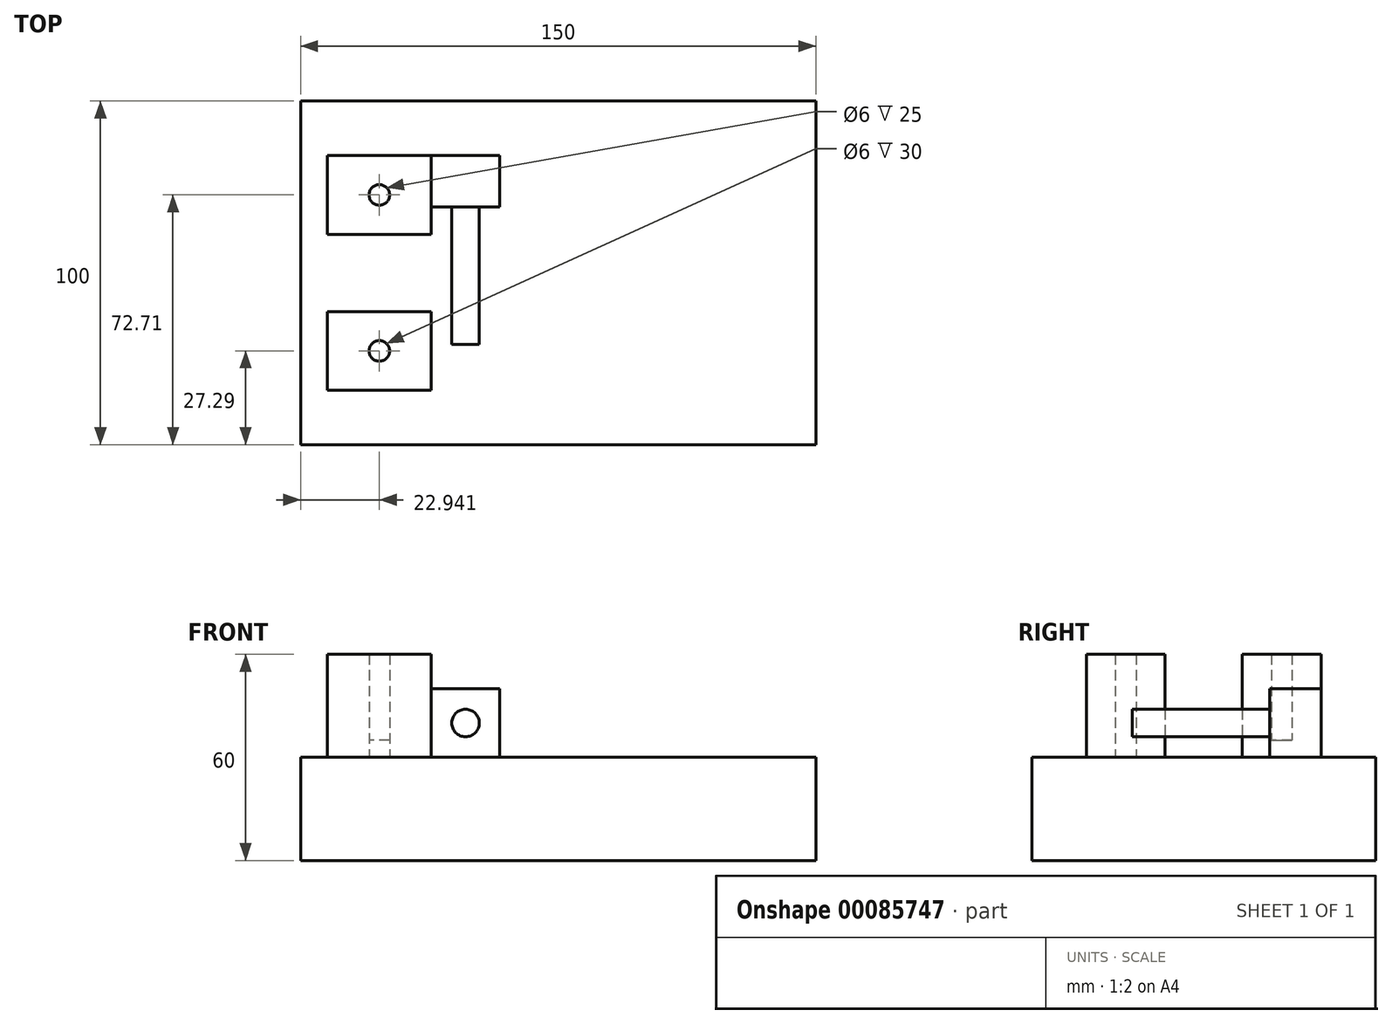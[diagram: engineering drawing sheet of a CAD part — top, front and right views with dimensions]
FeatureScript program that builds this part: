
annotation { "Feature Type Name" : "Feature", "Feature Type Description" : "" }
export const myFeature = defineFeature(function(context is Context, id is Id, definition is map)
    precondition{}
    {
        {
            var Q0;
            Q0=qCreatedBy(makeId("Top.planeOp"),FACE);
            var sketch = newSketch(context, id + "F0", { "sketchPlane" : qUnion([Q0])});
            skLineSegment(sketch, "E0.bottom", {"start": v(75, 50) * mm, "end": v(-75, 50) * mm});
            skLineSegment(sketch, "E0.top", {"start": v(75, -50) * mm, "end": v(-75, -50) * mm});
            skLineSegment(sketch, "E0.left", {"start": v(75, 50) * mm, "end": v(75, -50) * mm});
            skLineSegment(sketch, "E0.right", {"start": v(-75, 50) * mm, "end": v(-75, -50) * mm});
            skPoint(sketch, "E0.middle", {"position": v(0, 0) * mm});
            skSolve(sketch);
        }
        {
            var Q0;
            Q0=makeQuery(id+"F0.imprint","IMPRINT",FACE,{"disambiguationData":[TD([[makeQuery(id+"F0.imprint","IMPRINT",EDGE,{"derivedFrom":sQuery(id+"F0.wireOp",EDGE,"E0.bottom")}),1.0]])]});
            extrude(context, id + "F1", {"entities" : qUnion([Q0]), "depth" : 30 * mm});
        }
        {
            var Q0;
            Q0=makeQuery(id+"F1.opExtrude","CAP_FACE",FACE,{"disambiguationData":[OSD([sQuery(id+"F0.wireOp",EDGE,"E0.bottom"),sQuery(id+"F0.wireOp",EDGE,"E0.top"),sQuery(id+"F0.wireOp",EDGE,"E0.left"),sQuery(id+"F0.wireOp",EDGE,"E0.right")])],"isStart":false});
            var sketch = newSketch(context, id + "F2", { "sketchPlane" : qUnion([Q0])});
            skCircle(sketch, "E1", {"center": v(-52.06, 22.71) * mm, "radius": 3 * mm});
            skLineSegment(sketch, "E2", {"start": v(0, 0) * mm, "end": v(-75, 0) * mm});
            skCircle(sketch, "E3.MirrorC", {"center": v(-52.06, -22.71) * mm, "radius": 3 * mm});
            skLineSegment(sketch, "E4.bottom", {"start": v(-36.98, 34.17) * mm, "end": v(-67.14, 34.17) * mm});
            skLineSegment(sketch, "E4.top", {"start": v(-36.98, 11.25) * mm, "end": v(-67.14, 11.25) * mm});
            skLineSegment(sketch, "E4.left", {"start": v(-36.98, 34.17) * mm, "end": v(-36.98, 11.25) * mm});
            skLineSegment(sketch, "E4.right", {"start": v(-67.14, 34.17) * mm, "end": v(-67.14, 11.25) * mm});
            skLineSegment(sketch, "E5.MirrorCS", {"start": v(-36.98, -11.25) * mm, "end": v(-67.14, -11.25) * mm});
            skLineSegment(sketch, "E6.MirrorCS", {"start": v(-67.14, -34.17) * mm, "end": v(-67.14, -11.25) * mm});
            skLineSegment(sketch, "E7.MirrorCS", {"start": v(-36.98, -34.17) * mm, "end": v(-67.14, -34.17) * mm});
            skLineSegment(sketch, "E8.MirrorCS", {"start": v(-36.98, -34.17) * mm, "end": v(-36.98, -11.25) * mm});
            skSolve(sketch);
        }
        {
            var Q0;
            Q0=makeQuery(id+"F2.imprint","IMPRINT",FACE,{"disambiguationData":[TD([[makeQuery(id+"F2.imprint","IMPRINT",EDGE,{"derivedFrom":sQuery(id+"F2.wireOp",EDGE,"E3.MirrorC")}),-1.0]])]});
            var Q1;
            Q1=makeQuery(id+"F2.imprint","IMPRINT",FACE,{"disambiguationData":[TD([[makeQuery(id+"F2.imprint","IMPRINT",EDGE,{"derivedFrom":sQuery(id+"F2.wireOp",EDGE,"E1")}),1.0]])]});
            extrude(context, id + "F3", {"entities" : qUnion([Q0, Q1]), "operationType" : NewBodyOperationType.ADD, "depth" : 5 * mm});
        }
        {
            var Q0;
            Q0 = qSketchRegion(id + "F2", true);
            extrude(context, id + "F4", {"entities" : qUnion([Q0]), "operationType" : NewBodyOperationType.ADD, "depth" : 30 * mm});
        }
        {
            var Q0;
            Q0=makeQuery(id+"F4.opExtrude","SWEPT_FACE",FACE,{"disambiguationData":[OSD([sQuery(id+"F2.wireOp",EDGE,"E4.bottom")])]});
            var sketch = newSketch(context, id + "F5", { "sketchPlane" : qUnion([Q0])});
            skLineSegment(sketch, "E9.bottom", {"start": v(36.98, 30) * mm, "end": v(16.98, 30) * mm});
            skLineSegment(sketch, "E9.top", {"start": v(36.98, 50) * mm, "end": v(16.98, 50) * mm});
            skLineSegment(sketch, "E9.left", {"start": v(36.98, 30) * mm, "end": v(36.98, 50) * mm});
            skLineSegment(sketch, "E9.right", {"start": v(16.98, 30) * mm, "end": v(16.98, 50) * mm});
            skSolve(sketch);
        }
        {
            var Q0;
            Q0=makeQuery(id+"F5.imprint","IMPRINT",FACE,{"disambiguationData":[TD([[makeQuery(id+"F5.imprint","IMPRINT",EDGE,{"derivedFrom":sQuery(id+"F5.wireOp",EDGE,"E9.bottom")}),-1.0]])]});
            extrude(context, id + "F6", {"entities" : qUnion([Q0]), "operationType" : NewBodyOperationType.ADD, "oppositeDirection" : true, "depth" : 15 * mm});
        }
        {
            var Q0;
            Q0=makeQuery(id+"F6.opExtrude","CAP_FACE",FACE,{"disambiguationData":[OSD([sQuery(id+"F5.wireOp",EDGE,"E9.bottom"),sQuery(id+"F5.wireOp",EDGE,"E9.top"),sQuery(id+"F5.wireOp",EDGE,"E9.left"),sQuery(id+"F5.wireOp",EDGE,"E9.right")])],"isStart":false});
            var sketch = newSketch(context, id + "F7", { "sketchPlane" : qUnion([Q0])});
            skCircle(sketch, "E10", {"center": v(-26.98, 40) * mm, "radius": 4 * mm});
            skPoint(sketch, "E10.centerSnap0", {"position": v(-26.98, 50) * mm});
            skPoint(sketch, "E10.centerSnap1", {"position": v(-36.98, 40) * mm});
            skSolve(sketch);
        }
        {
            var Q0;
            Q0=makeQuery(id+"F7.imprint","IMPRINT",FACE,{"disambiguationData":[TD([[makeQuery(id+"F7.imprint","IMPRINT",EDGE,{"derivedFrom":sQuery(id+"F7.wireOp",EDGE,"E10")}),1.0]])]});
            extrude(context, id + "F8", {"entities" : qUnion([Q0]), "operationType" : NewBodyOperationType.ADD, "depth" : 40 * mm});
        }
    });
